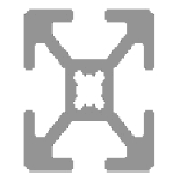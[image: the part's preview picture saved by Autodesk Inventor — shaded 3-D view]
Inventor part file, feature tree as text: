
AUTODESK INVENTOR PART (.ipt)
format: ipt  version: 2013 SP2 (Build 170200200, 200)  size: 233,472 bytes
history: native  units: in
note: dims shown in document units (in); Inventor stores cm internally (conversion verified against a paired STEP export)
features: other x5, sketch x3, plane x1
ambient origin geometry x8: Origin, YZ Plane, XZ Plane, XY Plane, X Axis, Y Axis, Z Axis, Center Point
bodies: Solid1 (feature_tree), Body (feature_tree)
feature tree (9):
  other  "Driven Length"
  other  "Frame Generator"
  other  "Blocks"
  other  "Start Plane"
  other  "End Plane"
  sketch  "Sketch"  dims[d4=0.13in d5=0.0in d6=90.0deg d7=16.5354in]
  sketch  "Sketch2"  dims[d2=0.7874in]
  plane  "Work Plane3"
  sketch  "Sketch3"  dims[d3=17.3228in]
